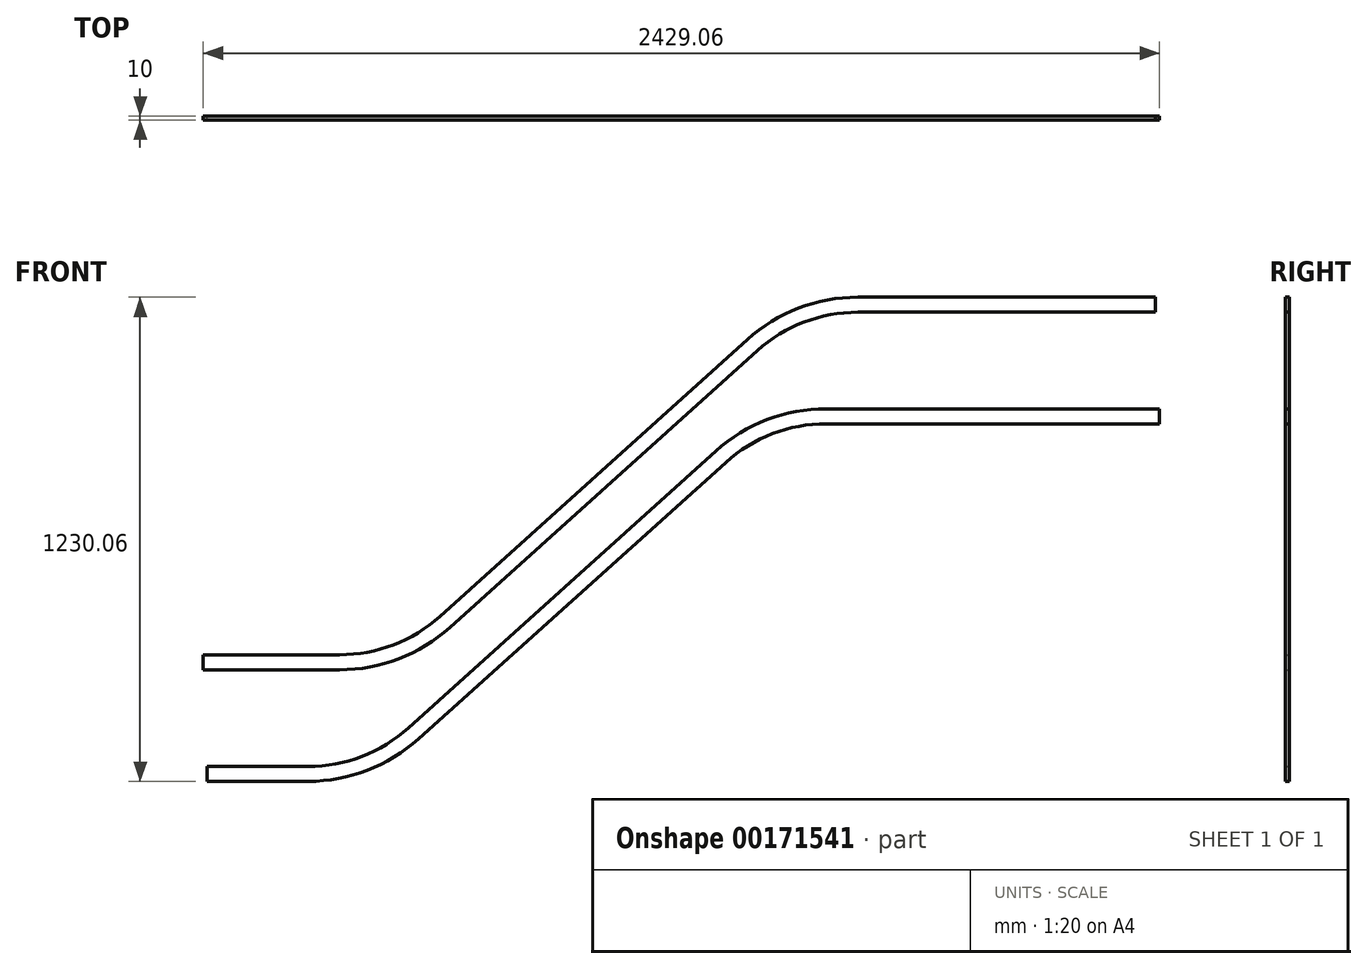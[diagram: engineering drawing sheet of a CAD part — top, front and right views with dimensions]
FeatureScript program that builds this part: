
annotation { "Feature Type Name" : "Feature", "Feature Type Description" : "" }
export const myFeature = defineFeature(function(context is Context, id is Id, definition is map)
    precondition{}
    {
        {
            var Q0;
            Q0=qCreatedBy(makeId("Front.planeOp"),FACE);
            var sketch = newSketch(context, id + "F0", { "sketchPlane" : qUnion([Q0])});
            skLineSegment(sketch, "E0", {"start": v(129.67, 109.8) * mm, "end": v(910.51, 812.88) * mm, "construction": true});
            skArc(sketch, "E1.0", {"start": v(1191.37, 1269.69) * mm, "mid": v(1191.37, 1269.69) * mm, "end": v(1191.36, 1269.69) * mm});
            skLineSegment(sketch, "E2", {"start": v(1191.36, 1269.69) * mm, "end": v(1191.37, 1269.69) * mm});
            skLineSegment(sketch, "E3", {"start": v(-404.44, 290.56) * mm, "end": v(-57.98, 290.56) * mm, "construction": true});
            skLineSegment(sketch, "E4", {"start": v(-394.44, 7.06) * mm, "end": v(-137.98, 7.06) * mm, "construction": true});
            skLineSegment(sketch, "E5", {"start": v(1178.16, 915.62) * mm, "end": v(2024.62, 915.62) * mm, "construction": true});
            skLineSegment(sketch, "E6", {"start": v(1258.16, 1199.12) * mm, "end": v(2014.62, 1199.12) * mm, "construction": true});
            skPoint(sketch, "E7", {"position": v(-404.44, 309.56) * mm});
            skPoint(sketch, "E8", {"position": v(-404.44, 271.56) * mm});
            skPoint(sketch, "E9", {"position": v(-394.44, 26.06) * mm});
            skPoint(sketch, "E10", {"position": v(-394.44, -11.94) * mm});
            skPoint(sketch, "E11", {"position": v(2024.62, 896.62) * mm});
            skPoint(sketch, "E12", {"position": v(2024.62, 934.62) * mm});
            skPoint(sketch, "E13", {"position": v(2014.62, 1180.12) * mm});
            skPoint(sketch, "E14", {"position": v(2014.62, 1218.12) * mm});
            skPoint(sketch, "E15.visualSharp", {"position": v(95.56, 290.56) * mm});
            skPoint(sketch, "E16.visualSharp", {"position": v(15.56, 7.06) * mm});
            skPoint(sketch, "E17.visualSharp", {"position": v(1024.62, 915.62) * mm});
            skPoint(sketch, "E18.visualSharp", {"position": v(1104.62, 1199.12) * mm});
            skLineSegment(sketch, "E19", {"start": v(-404.44, 271.56) * mm, "end": v(-404.44, 309.56) * mm});
            skLineSegment(sketch, "E20", {"start": v(-394.44, 26.06) * mm, "end": v(-394.44, -11.94) * mm});
            skLineSegment(sketch, "E21", {"start": v(2024.62, 896.62) * mm, "end": v(2024.62, 934.62) * mm});
            skLineSegment(sketch, "E22", {"start": v(2014.62, 1180.12) * mm, "end": v(2014.62, 1218.12) * mm});
            skLineSegment(sketch, "E23", {"start": v(572.56, 720.05) * mm, "end": v(572.56, 508.58) * mm, "construction": true});
            skLineSegment(sketch, "E24", {"start": v(209.67, 393.3) * mm, "end": v(990.51, 1096.38) * mm, "construction": true});
            skArc(sketch, "E25.filletArc", {"start": v(-137.98, 7.06) * mm, "mid": v(5.37, 33.63) * mm, "end": v(129.67, 109.8) * mm, "construction": true});
            skArc(sketch, "E26.filletArc", {"start": v(-57.98, 290.56) * mm, "mid": v(85.37, 317.13) * mm, "end": v(209.67, 393.3) * mm, "construction": true});
            skArc(sketch, "E27.filletArc", {"start": v(1178.16, 915.62) * mm, "mid": v(1034.82, 889.05) * mm, "end": v(910.51, 812.88) * mm, "construction": true});
            skArc(sketch, "E28.filletArc", {"start": v(1258.16, 1199.12) * mm, "mid": v(1114.82, 1172.55) * mm, "end": v(990.51, 1096.38) * mm, "construction": true});
            skArc(sketch, "E29.0", {"start": v(-137.98, -11.94) * mm, "mid": v(12.18, 15.9) * mm, "end": v(142.39, 95.69) * mm});
            skArc(sketch, "E30.0", {"start": v(-137.98, 26.06) * mm, "mid": v(-1.44, 51.37) * mm, "end": v(116.96, 123.93) * mm});
            skArc(sketch, "E31.0", {"start": v(1178.16, 934.62) * mm, "mid": v(1028, 906.8) * mm, "end": v(897.8, 827) * mm});
            skArc(sketch, "E32.0", {"start": v(1178.16, 896.62) * mm, "mid": v(1041.63, 871.31) * mm, "end": v(923.23, 798.76) * mm});
            skArc(sketch, "E33.0", {"start": v(1258.16, 1218.12) * mm, "mid": v(1108, 1190.3) * mm, "end": v(977.8, 1110.5) * mm});
            skArc(sketch, "E34.0", {"start": v(1258.16, 1180.12) * mm, "mid": v(1121.63, 1154.81) * mm, "end": v(1003.23, 1082.26) * mm});
            skArc(sketch, "E35.0", {"start": v(-57.98, 271.56) * mm, "mid": v(92.18, 299.4) * mm, "end": v(222.39, 379.19) * mm});
            skArc(sketch, "E36.0", {"start": v(-57.98, 309.56) * mm, "mid": v(78.56, 334.87) * mm, "end": v(196.96, 407.43) * mm});
            skLineSegment(sketch, "E37", {"start": v(-57.98, 271.56) * mm, "end": v(-404.44, 271.56) * mm});
            skLineSegment(sketch, "E38", {"start": v(-57.98, 309.56) * mm, "end": v(-404.44, 309.56) * mm});
            skLineSegment(sketch, "E39", {"start": v(222.39, 379.19) * mm, "end": v(1003.23, 1082.26) * mm});
            skLineSegment(sketch, "E40", {"start": v(196.96, 407.43) * mm, "end": v(977.8, 1110.5) * mm});
            skLineSegment(sketch, "E41", {"start": v(-137.98, -11.94) * mm, "end": v(-394.44, -11.94) * mm});
            skLineSegment(sketch, "E42", {"start": v(-394.44, 26.06) * mm, "end": v(-137.98, 26.06) * mm});
            skLineSegment(sketch, "E43", {"start": v(142.39, 95.69) * mm, "end": v(923.23, 798.76) * mm});
            skLineSegment(sketch, "E44", {"start": v(897.8, 827) * mm, "end": v(116.96, 123.93) * mm});
            skLineSegment(sketch, "E45", {"start": v(1178.16, 896.62) * mm, "end": v(2024.62, 896.62) * mm});
            skLineSegment(sketch, "E46", {"start": v(2024.62, 934.62) * mm, "end": v(1178.16, 934.62) * mm});
            skLineSegment(sketch, "E47", {"start": v(1258.16, 1180.12) * mm, "end": v(2014.62, 1180.12) * mm});
            skLineSegment(sketch, "E48", {"start": v(2014.62, 1218.12) * mm, "end": v(1258.16, 1218.12) * mm});
            skSolve(sketch);
        }
        {
            var Q0;
            Q0=qSketchRegion(id+"F0",true);
            extrude(context, id + "F1", {"entities" : qUnion([Q0]), "depth" : 10 * mm});
        }
    });
